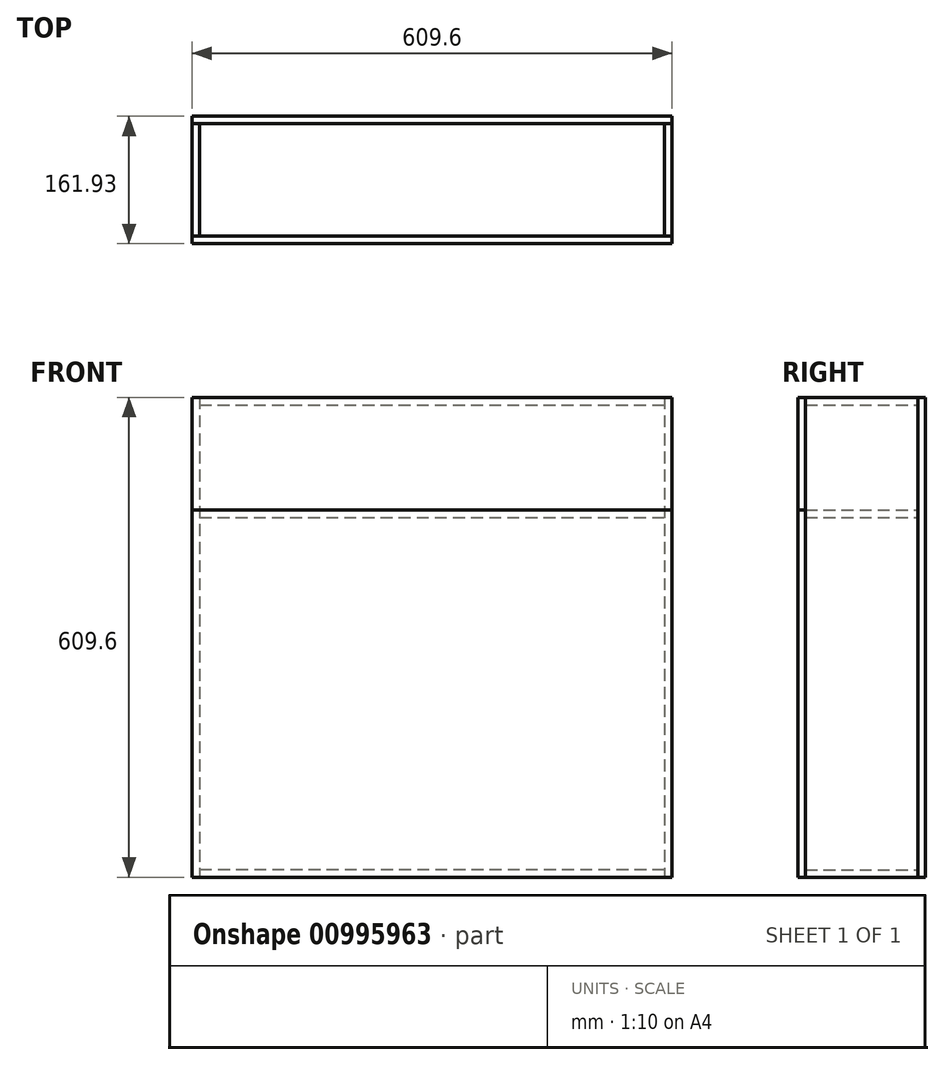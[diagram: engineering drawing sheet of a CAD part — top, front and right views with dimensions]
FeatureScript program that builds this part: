
annotation { "Feature Type Name" : "Feature", "Feature Type Description" : "" }
export const myFeature = defineFeature(function(context is Context, id is Id, definition is map)
    precondition{}
    {
        {
            var Q0;
            Q0=qCreatedBy(makeId("Front.planeOp"),FACE);
            var sketch = newSketch(context, id + "F0", { "sketchPlane" : qUnion([Q0])});
            skLineSegment(sketch, "E0.bottom", {"start": v(304.8, 304.8) * mm, "end": v(-304.8, 304.8) * mm});
            skLineSegment(sketch, "E0.top", {"start": v(304.8, -304.8) * mm, "end": v(-304.8, -304.8) * mm});
            skLineSegment(sketch, "E0.left", {"start": v(304.8, 304.8) * mm, "end": v(304.8, -304.8) * mm});
            skLineSegment(sketch, "E0.right", {"start": v(-304.8, 304.8) * mm, "end": v(-304.8, -304.8) * mm});
            skPoint(sketch, "E0.middle", {"position": v(0, 0) * mm});
            skSolve(sketch);
        }
        {
            var Q0;
            Q0 = qSketchRegion(id + "F0", true);
            extrude(context, id + "F1", {"entities" : qUnion([Q0]), "depth" : 9.52 * mm, "offsetDistance" : 25.4 * mm});
        }
        {
            var Q0;
            Q0=makeQuery(id+"F1.opExtrude","CAP_FACE",FACE,{"disambiguationData":[OSD([sQuery(id+"F0.wireOp",EDGE,"E0.bottom"),sQuery(id+"F0.wireOp",EDGE,"E0.top"),sQuery(id+"F0.wireOp",EDGE,"E0.left"),sQuery(id+"F0.wireOp",EDGE,"E0.right")])],"isStart":false});
            var sketch = newSketch(context, id + "F2", { "sketchPlane" : qUnion([Q0])});
            skLineSegment(sketch, "E1.bottom", {"start": v(-304.8, 304.8) * mm, "end": v(-295.28, 304.8) * mm});
            skLineSegment(sketch, "E1.top", {"start": v(-304.8, -304.8) * mm, "end": v(-295.27, -304.8) * mm});
            skLineSegment(sketch, "E1.left", {"start": v(-304.8, 304.8) * mm, "end": v(-304.8, -304.8) * mm});
            skLineSegment(sketch, "E1.right", {"start": v(-295.28, 304.8) * mm, "end": v(-295.28, -304.8) * mm});
            skSolve(sketch);
        }
        {
            var Q0;
            Q0 = qSketchRegion(id + "F2", true);
            extrude(context, id + "F3", {"entities" : qUnion([Q0]), "depth" : 142.88 * mm, "offsetDistance" : 25.4 * mm});
        }
        {
            var Q0;
            Q0=makeQuery(id+"F3.opExtrude","SWEPT_BODY",BODY,{"disambiguationData":[OSD([sQuery(id+"F2.wireOp",EDGE,"E1.bottom"),sQuery(id+"F2.wireOp",EDGE,"E1.top"),sQuery(id+"F2.wireOp",EDGE,"E1.left"),sQuery(id+"F2.wireOp",EDGE,"E1.right")])]});
            var Q1;
            Q1=qCreatedBy(makeId("Right.planeOp"),FACE);
            mirror(context, id + "F4", {"entities" : qUnion([Q0]), "mirrorPlane" : qUnion([Q1])});
        }
        {
            var Q0;
            Q0=makeQuery(id+"F1.opExtrude","CAP_FACE",FACE,{"disambiguationData":[OSD([sQuery(id+"F0.wireOp",EDGE,"E0.bottom"),sQuery(id+"F0.wireOp",EDGE,"E0.top"),sQuery(id+"F0.wireOp",EDGE,"E0.left"),sQuery(id+"F0.wireOp",EDGE,"E0.right")])],"isStart":false});
            var sketch = newSketch(context, id + "F5", { "sketchPlane" : qUnion([Q0])});
            skLineSegment(sketch, "E2.bottom", {"start": v(-295.28, 304.8) * mm, "end": v(295.28, 304.8) * mm});
            skLineSegment(sketch, "E2.top", {"start": v(-295.28, 295.28) * mm, "end": v(295.28, 295.28) * mm});
            skLineSegment(sketch, "E2.left", {"start": v(-295.28, 304.8) * mm, "end": v(-295.28, 295.28) * mm});
            skLineSegment(sketch, "E2.right", {"start": v(295.28, 304.8) * mm, "end": v(295.28, 295.28) * mm});
            skSolve(sketch);
        }
        {
            var Q0;
            Q0 = qSketchRegion(id + "F5", true);
            extrude(context, id + "F6", {"entities" : qUnion([Q0]), "depth" : 142.88 * mm, "offsetDistance" : 25.4 * mm});
        }
        {
            var Q0;
            Q0=makeQuery(id+"F6.opExtrude","SWEPT_BODY",BODY,{"disambiguationData":[OSD([sQuery(id+"F5.wireOp",EDGE,"E2.bottom"),sQuery(id+"F5.wireOp",EDGE,"E2.top"),sQuery(id+"F5.wireOp",EDGE,"E2.left"),sQuery(id+"F5.wireOp",EDGE,"E2.right")])]});
            transform(context, id + "F7", {"entities" : qUnion([Q0]), "transformType" : TransformType.TRANSLATION_3D, "dx" : 0 * mm, "dy" : 0 * mm, "dz" : -142.88 * mm, "makeCopy" : true});
        }
        {
            var Q0;
            Q0=makeQuery(id+"F6.opExtrude","SWEPT_BODY",BODY,{"disambiguationData":[OSD([sQuery(id+"F5.wireOp",EDGE,"E2.bottom"),sQuery(id+"F5.wireOp",EDGE,"E2.top"),sQuery(id+"F5.wireOp",EDGE,"E2.left"),sQuery(id+"F5.wireOp",EDGE,"E2.right")])]});
            transform(context, id + "F8", {"entities" : qUnion([Q0]), "transformType" : TransformType.TRANSLATION_3D, "dx" : 0 * mm, "dy" : 0 * mm, "dz" : -600.07 * mm, "makeCopy" : true});
        }
        {
            var Q0;
            Q0=makeQuery(id+"F6.opExtrude","CAP_FACE",FACE,{"disambiguationData":[OSD([sQuery(id+"F5.wireOp",EDGE,"E2.bottom"),sQuery(id+"F5.wireOp",EDGE,"E2.top"),sQuery(id+"F5.wireOp",EDGE,"E2.left"),sQuery(id+"F5.wireOp",EDGE,"E2.right")])],"isStart":false});
            var sketch = newSketch(context, id + "F9", { "sketchPlane" : qUnion([Q0])});
            skLineSegment(sketch, "E3.bottom", {"start": v(-295.28, 304.8) * mm, "end": v(304.8, 304.8) * mm});
            skLineSegment(sketch, "E3.top", {"start": v(-304.8, 161.93) * mm, "end": v(304.8, 161.93) * mm});
            skLineSegment(sketch, "E3.left", {"start": v(-304.8, 304.8) * mm, "end": v(-304.8, 161.93) * mm});
            skLineSegment(sketch, "E3.right", {"start": v(304.8, 304.8) * mm, "end": v(304.8, 161.93) * mm});
            skLineSegment(sketch, "E4", {"start": v(-304.8, 304.8) * mm, "end": v(-295.28, 304.8) * mm});
            skSolve(sketch);
        }
        {
            var Q0;
            Q0 = qSketchRegion(id + "F9", true);
            extrude(context, id + "F10", {"entities" : qUnion([Q0]), "depth" : 9.52 * mm, "offsetDistance" : 25.4 * mm});
        }
        {
            var Q0;
            Q0=makeQuery(id+"F3.opExtrude","CAP_FACE",FACE,{"disambiguationData":[OSD([sQuery(id+"F2.wireOp",EDGE,"E1.bottom"),sQuery(id+"F2.wireOp",EDGE,"E1.top"),sQuery(id+"F2.wireOp",EDGE,"E1.left"),sQuery(id+"F2.wireOp",EDGE,"E1.right")])],"isStart":false});
            var sketch = newSketch(context, id + "F11", { "sketchPlane" : qUnion([Q0])});
            skLineSegment(sketch, "E5.bottom", {"start": v(-304.8, 161.93) * mm, "end": v(304.8, 161.93) * mm});
            skLineSegment(sketch, "E5.top", {"start": v(-304.8, -304.8) * mm, "end": v(304.8, -304.8) * mm});
            skLineSegment(sketch, "E5.left", {"start": v(-304.8, 161.93) * mm, "end": v(-304.8, -304.8) * mm});
            skLineSegment(sketch, "E5.right", {"start": v(304.8, 161.93) * mm, "end": v(304.8, -304.8) * mm});
            skSolve(sketch);
        }
        {
            var Q0;
            Q0 = qSketchRegion(id + "F11", true);
            extrude(context, id + "F12", {"entities" : qUnion([Q0]), "depth" : 9.52 * mm, "offsetDistance" : 25.4 * mm});
        }
    });
